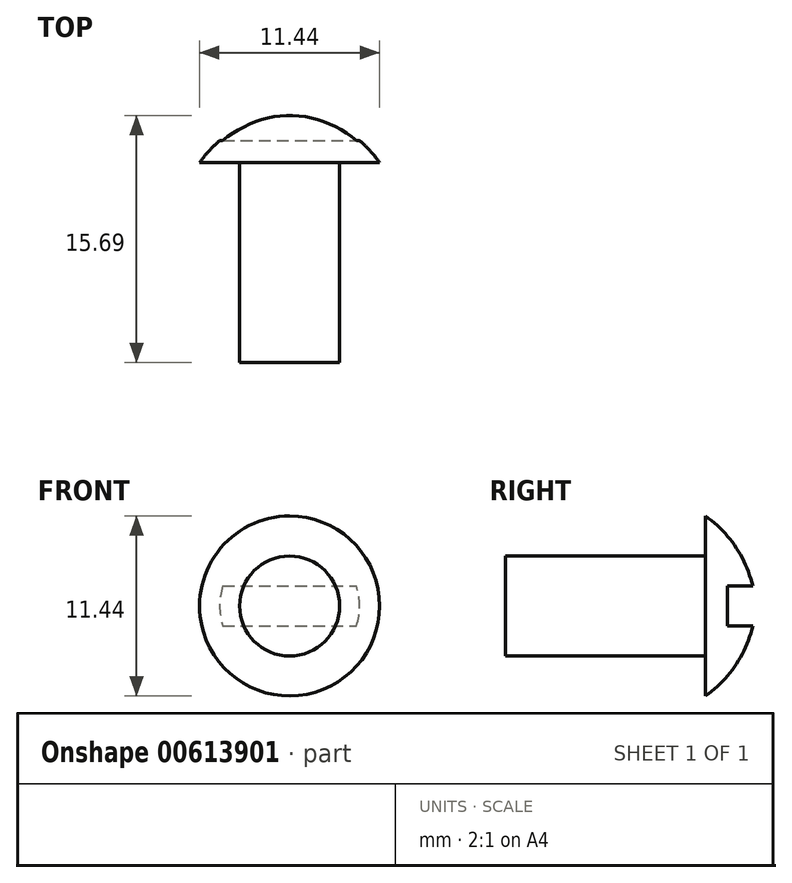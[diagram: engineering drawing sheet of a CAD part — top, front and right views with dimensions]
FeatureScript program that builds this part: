
annotation { "Feature Type Name" : "Feature", "Feature Type Description" : "" }
export const myFeature = defineFeature(function(context is Context, id is Id, definition is map)
    precondition{}
    {
        {
            var Q0;
            Q0=qCreatedBy(makeId("Top.planeOp"),FACE);
            var sketch = newSketch(context, id + "F0", { "sketchPlane" : qUnion([Q0])});
            skLineSegment(sketch, "E0", {"start": v(0, 0) * mm, "end": v(3.17, 0) * mm});
            skLineSegment(sketch, "E1", {"start": v(3.17, 0) * mm, "end": v(3.17, 12.7) * mm});
            skLineSegment(sketch, "E2", {"start": v(3.17, 12.7) * mm, "end": v(5.72, 12.7) * mm});
            skPoint(sketch, "E3.start.orphan", {"position": v(0, 7.82) * mm});
            skArc(sketch, "E4", {"start": v(5.72, 12.7) * mm, "mid": v(3.22, 14.94) * mm, "end": v(0, 15.88) * mm});
            skLineSegment(sketch, "E5", {"start": v(0, 15.88) * mm, "end": v(0, 0) * mm});
            skSolve(sketch);
        }
        {
            var Q0;
            Q0=makeQuery(id+"F0.imprint","IMPRINT",FACE,{"disambiguationData":[TD([[makeQuery(id+"F0.imprint","IMPRINT",EDGE,{"derivedFrom":sQuery(id+"F0.wireOp",EDGE,"E0")}),1.0]])]});
            var Q1;
            Q1=sQuery(id+"F0.wireOp",EDGE,"E5");
            revolve(context, id + "F1", {"entities" : qUnion([Q0]), "axis" : qUnion([Q1]), "revolveType" : RevolveType.FULL});
        }
        {
            var Q0;
            Q0=makeQuery(id+"F1.opRevolve","SWEPT_FACE",FACE,{"disambiguationData":[OSD([sQuery(id+"F0.wireOp",EDGE,"E2")])]});
            cPlane(context, id + "F2", {"entities" : qUnion([Q0]), "cplaneType" : CPlaneType.OFFSET, "offset" : 1.4 * mm, "oppositeDirection" : true, "width" : 152.4 * mm, "height" : 152.4 * mm});
        }
        {
            var Q0;
            Q0=qCreatedBy(id+"F2.planeOp",FACE);
            var sketch = newSketch(context, id + "F3", { "sketchPlane" : qUnion([Q0])});
            skLineSegment(sketch, "E6.bottom", {"start": v(-5.08, 1.27) * mm, "end": v(5.08, 1.27) * mm});
            skLineSegment(sketch, "E6.top", {"start": v(-5.08, -1.27) * mm, "end": v(5.08, -1.27) * mm});
            skLineSegment(sketch, "E6.left", {"start": v(-5.08, 1.27) * mm, "end": v(-5.08, -1.27) * mm});
            skLineSegment(sketch, "E6.right", {"start": v(5.08, 1.27) * mm, "end": v(5.08, -1.27) * mm});
            skPoint(sketch, "E6.middle", {"position": v(0, 0) * mm});
            skSolve(sketch);
        }
        {
            var Q0;
            Q0 = qSketchRegion(id + "F3", true);
            extrude(context, id + "F4", {"entities" : qUnion([Q0]), "operationType" : NewBodyOperationType.REMOVE, "oppositeDirection" : true, "depth" : 22.56 * mm, "offsetDistance" : 25.4 * mm});
        }
    });
